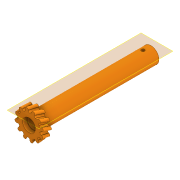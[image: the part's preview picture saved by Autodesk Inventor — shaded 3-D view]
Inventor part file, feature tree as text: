
AUTODESK INVENTOR PART (.ipt)
format: ipt  version: 2020 (Build 240168000, 168)  size: 355,840 bytes
history: native  units: in
note: dims shown in document units (in); Inventor stores cm internally (conversion verified against a paired STEP export)
features: sketch x6, extrude x4, plane x3, sweep x1, other x1, projected_geometry x1
ambient origin geometry x8: Origin, YZ Plane, XZ Plane, XY Plane, X Axis, Y Axis, Z Axis, Center Point
bodies: Solid1 (feature_tree)
feature tree (16):
  extrude  "Extrusion1"  Depth=0.3937in
  plane  "Work Plane1"
  sweep  "Sweep1"
  extrude  "Extrusion3"  Depth=0.0866in
  plane  "Work Plane2"
  extrude  "Extrusion4"  Depth=0.0787in
  plane  "Work Plane3"
  extrude  "Extrusion5"  Depth=2.7953in TaperAngle=360.0deg
  sketch  "Sketch1"  dims[d0=0.3937in d1=0.315in]
  sketch  "Sketch3"  dims[d2=2.9921in d3=0.0in d7=-0.1969in]
  sketch  "3D Sketch1"
  other  "Helical Curve1"
  sketch  "Sketch4"  dims[d8=0.7087in d9=0.0866in]
  sketch  "Sketch5"  dims[d10=0.0787in d11=0.0787in]
  sketch  "Sketch6"  dims[d12=0.0787in d13=4.7244in d15=360.0deg d17=0.1969in d18=0.0118in d19=0.535in d20=0.0in d21=0.0in d22=0.0in d23=0.1969in d25=0.0787in d26=2.9921in d27=0.0in d28=-0.0984in d29=0.2756in d30=2.7953in d31=0.0in d32=0.1969in d33=2.9921in d34=0.0in d24=0.0344in]
  projected_geometry  "Projected Loop1"
